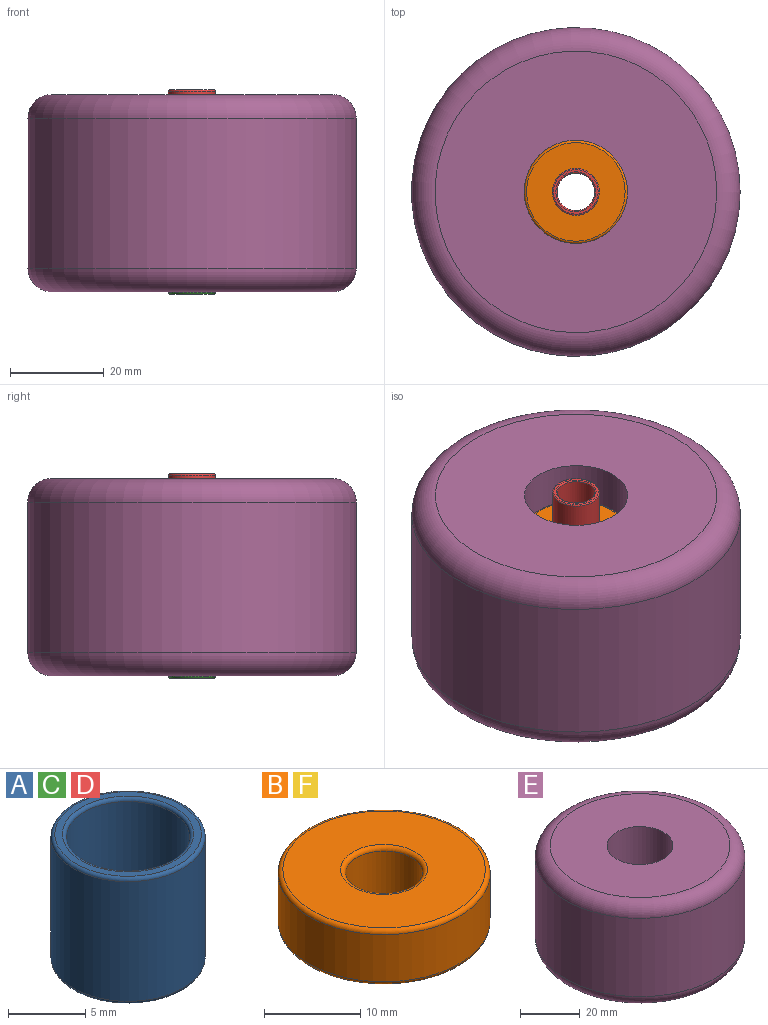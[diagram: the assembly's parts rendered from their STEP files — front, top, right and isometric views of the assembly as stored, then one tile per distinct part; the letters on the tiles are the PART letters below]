
ASSEMBLY  parts=6 mates=12
PART A: 8 faces, bbox 10.8x10.8x10 mm
  f0: cylinder r=4mm len=9.5mm, axis (0,0,-1), area 238.8mm2, adj f4,f6
  f1: cylinder r=5mm len=10mm, axis (0,0,-1), area 298.5mm2, adj f5,f7
  f2: plane 9.5x9.5mm, normal (0,0,1), area 14.1mm2, adj f6,f7
  f3: plane 9.5x9.5mm, normal (0,0,-1), area 14.1mm2, adj f4,f5
  f4: torus R=4.25mm, axis (0,0,1), area 10.1mm2, adj f0,f3
  f5: torus R=4.75mm, axis (0,0,1), area 12.1mm2, adj f1,f3
  f6: torus R=4.25mm, axis (0,0,1), area 10.1mm2, adj f0,f2
  f7: torus R=4.75mm, axis (0,0,1), area 12.1mm2, adj f1,f2
PART B: 8 faces, bbox 23.8x23.8x7 mm
  f0: cylinder r=4mm len=8mm, axis (0,0,-1), area 150.8mm2, adj f4,f6
  f1: cylinder r=11mm len=22mm, axis (0,0,-1), area 414.7mm2, adj f5,f7
  f2: plane 21x21mm, normal (0,0,1), area 282.7mm2, adj f6,f7
  f3: plane 21x21mm, normal (0,0,-1), area 282.7mm2, adj f4,f5
  f4: torus R=4.5mm, axis (0,0,1), area 20.6mm2, adj f0,f3
  f5: torus R=10.5mm, axis (0,0,1), area 53.4mm2, adj f1,f3
  f6: torus R=4.5mm, axis (0,0,1), area 20.6mm2, adj f0,f2
  f7: torus R=10.5mm, axis (0,0,1), area 53.4mm2, adj f1,f2
PART C: same geometry as A
PART D: same geometry as A
PART E: 10 faces, bbox 75.8x75.8x42 mm
  f0: plane 60x60mm, normal (0,0,-1), area 2447.3mm2, adj f6,f8
  f1: cylinder r=6mm len=12mm, axis (0,0,1), area 377mm2, adj f5,f7
  f2: cylinder r=35mm len=70mm, axis (0,0,-1), area 7037.2mm2, adj f8,f9
  f3: plane 60x60mm, normal (0,0,1), area 2447.3mm2, adj f4,f9
  f4: cylinder r=11mm len=22mm, axis (0,0,1), area 1105.8mm2, adj f3,f5
  f5: plane 22x22mm, normal (0,0,1), area 267mm2, adj f1,f4
  f6: cylinder r=11mm len=22mm, axis (0,0,-1), area 1105.8mm2, adj f0,f7
  f7: plane 22x22mm, normal (0,0,-1), area 267mm2, adj f1,f6
  f8: torus R=30mm, axis (0,0,1), area 1637.5mm2, adj f0,f2
  f9: torus R=30mm, axis (0,0,1), area 1637.5mm2, adj f2,f3
PART F: same geometry as B
PLACE A t=(-21.08,-21.21,-3.19)mm
PLACE B rot(axis=(1,0,0),180deg) t=(-21.08,-21.21,5.31)mm
PLACE C rot(axis=(1,0,0),180deg) t=(-21.08,-21.21,-19.69)mm
PLACE D t=(-21.08,-21.21,13.81)mm
PLACE E t=(-21.08,-21.21,-3.19)mm fixed
PLACE F t=(-21.08,-21.21,-11.69)mm
MATE slider D.f1 <-> E.f2  axis (0,0,-1) through (-21.08,-21.21,18.56)mm
MATE planar B.f1 <-> D.f1  axis (0,0,1) through (-21.08,-21.21,8.81)mm
MATE slider E.f1 <-> B.f1  axis (0,0,1) through (-21.08,-21.21,17.81)mm
MATE parallel A.f1 <-> E.f1  axis (0,0,1) through (-21.08,-21.21,1.81)mm
MATE parallel A.f1 <-> F.f1  axis (0,0,-1) through (-21.08,-21.21,-8.19)mm
MATE planar F.f1 <-> E.f1  axis (0,0,1) through (-21.08,-21.21,-8.19)mm
MATE planar F.f1 <-> A.f1  axis (0,0,1) through (-21.08,-21.21,-8.19)mm
MATE slider E.f1 <-> A.f0  axis (0,0,1) through (-21.08,-21.21,17.81)mm
MATE planar F.f0 <-> C.f1  axis (0,0,1) through (-21.08,-21.21,-14.69)mm
MATE planar A.f1 <-> B.f1  axis (0,0,1) through (-21.08,-21.21,1.81)mm
MATE slider C.f0 <-> E.f1  axis (0,0,1) through (-21.08,-21.21,-24.44)mm
MATE slider F.f0 <-> E.f2  axis (0,0,1) through (-21.08,-21.21,-14.69)mm
